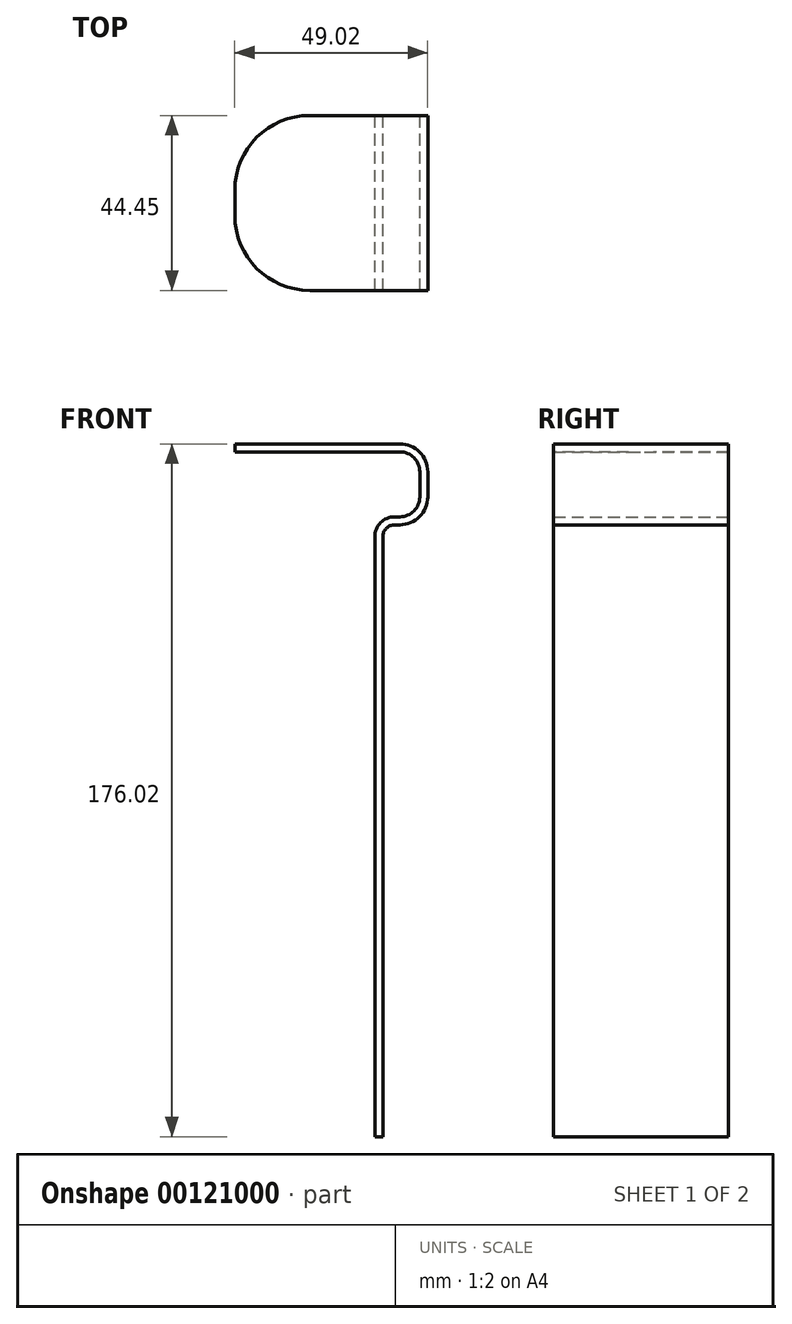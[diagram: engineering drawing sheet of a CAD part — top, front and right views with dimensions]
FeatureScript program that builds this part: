
annotation { "Feature Type Name" : "Feature", "Feature Type Description" : "" }
export const myFeature = defineFeature(function(context is Context, id is Id, definition is map)
    precondition{}
    {
        {
            var Q0;
            Q0=qCreatedBy(makeId("Front.planeOp"),FACE);
            var sketch = newSketch(context, id + "F0", { "sketchPlane" : qUnion([Q0])});
            skLineSegment(sketch, "E0", {"start": v(-39, 63.84) * mm, "end": v(2.9, 63.84) * mm});
            skPoint(sketch, "E1.visualSharp", {"position": v(15.14, 63.84) * mm});
            skArc(sketch, "E1.filletArc", {"start": v(7.98, 58.76) * mm, "mid": v(6.5, 62.35) * mm, "end": v(2.9, 63.84) * mm});
            skLineSegment(sketch, "E2", {"start": v(7.98, 58.76) * mm, "end": v(7.98, 52.41) * mm});
            skLineSegment(sketch, "E3", {"start": v(2.9, 47.33) * mm, "end": v(1.63, 47.33) * mm});
            skLineSegment(sketch, "E4", {"start": v(-3.45, 42.25) * mm, "end": v(-3.45, -110.15) * mm});
            skPoint(sketch, "E5.visualSharp", {"position": v(7.98, 47.33) * mm});
            skArc(sketch, "E5.filletArc", {"start": v(2.9, 47.33) * mm, "mid": v(6.5, 48.82) * mm, "end": v(7.98, 52.41) * mm});
            skArc(sketch, "E6.filletArc", {"start": v(1.63, 47.33) * mm, "mid": v(-1.96, 45.84) * mm, "end": v(-3.45, 42.25) * mm});
            skArc(sketch, "E7.0", {"start": v(2.9, 45.3) * mm, "mid": v(7.93, 47.38) * mm, "end": v(10.01, 52.41) * mm});
            skLineSegment(sketch, "E7.1", {"start": v(10.01, 58.76) * mm, "end": v(10.01, 52.41) * mm});
            skArc(sketch, "E7.2", {"start": v(10.01, 58.76) * mm, "mid": v(7.93, 63.8) * mm, "end": v(2.9, 65.87) * mm});
            skLineSegment(sketch, "E7.3", {"start": v(-39, 65.87) * mm, "end": v(2.9, 65.87) * mm});
            skLineSegment(sketch, "E8.0", {"start": v(-1.42, 42.25) * mm, "end": v(-1.42, -110.15) * mm});
            skArc(sketch, "E8.1", {"start": v(1.63, 45.3) * mm, "mid": v(-0.52, 44.4) * mm, "end": v(-1.42, 42.25) * mm});
            skLineSegment(sketch, "E8.2", {"start": v(2.9, 45.3) * mm, "end": v(1.63, 45.3) * mm});
            skLineSegment(sketch, "E9", {"start": v(-39, 65.87) * mm, "end": v(-39, 63.84) * mm});
            skLineSegment(sketch, "E10", {"start": v(-1.42, -110.15) * mm, "end": v(-3.45, -110.15) * mm});
            skSolve(sketch);
        }
        {
            var Q0;
            Q0=qSketchRegion(id+"F0",true);
            extrude(context, id + "F1", {"entities" : qUnion([Q0]), "depth" : 44.45 * mm});
        }
        {
            var Q0;
            Q0=makeQuery(id+"F1.opExtrude","CAP_EDGE",EDGE,{"disambiguationData":[OSD([sQuery(id+"F0.wireOp",EDGE,"E9")])],"isStart":true});
            var Q1;
            Q1=makeQuery(id+"F1.opExtrude","CAP_EDGE",EDGE,{"disambiguationData":[OSD([sQuery(id+"F0.wireOp",EDGE,"E9")])],"isStart":false});
            fillet(context, id + "F2", {"entities" : qUnion([Q0, Q1]), "radius" : 19.05 * mm, "tangentPropagation" : true, "allowEdgeOverflow" : false});
        }
    });
